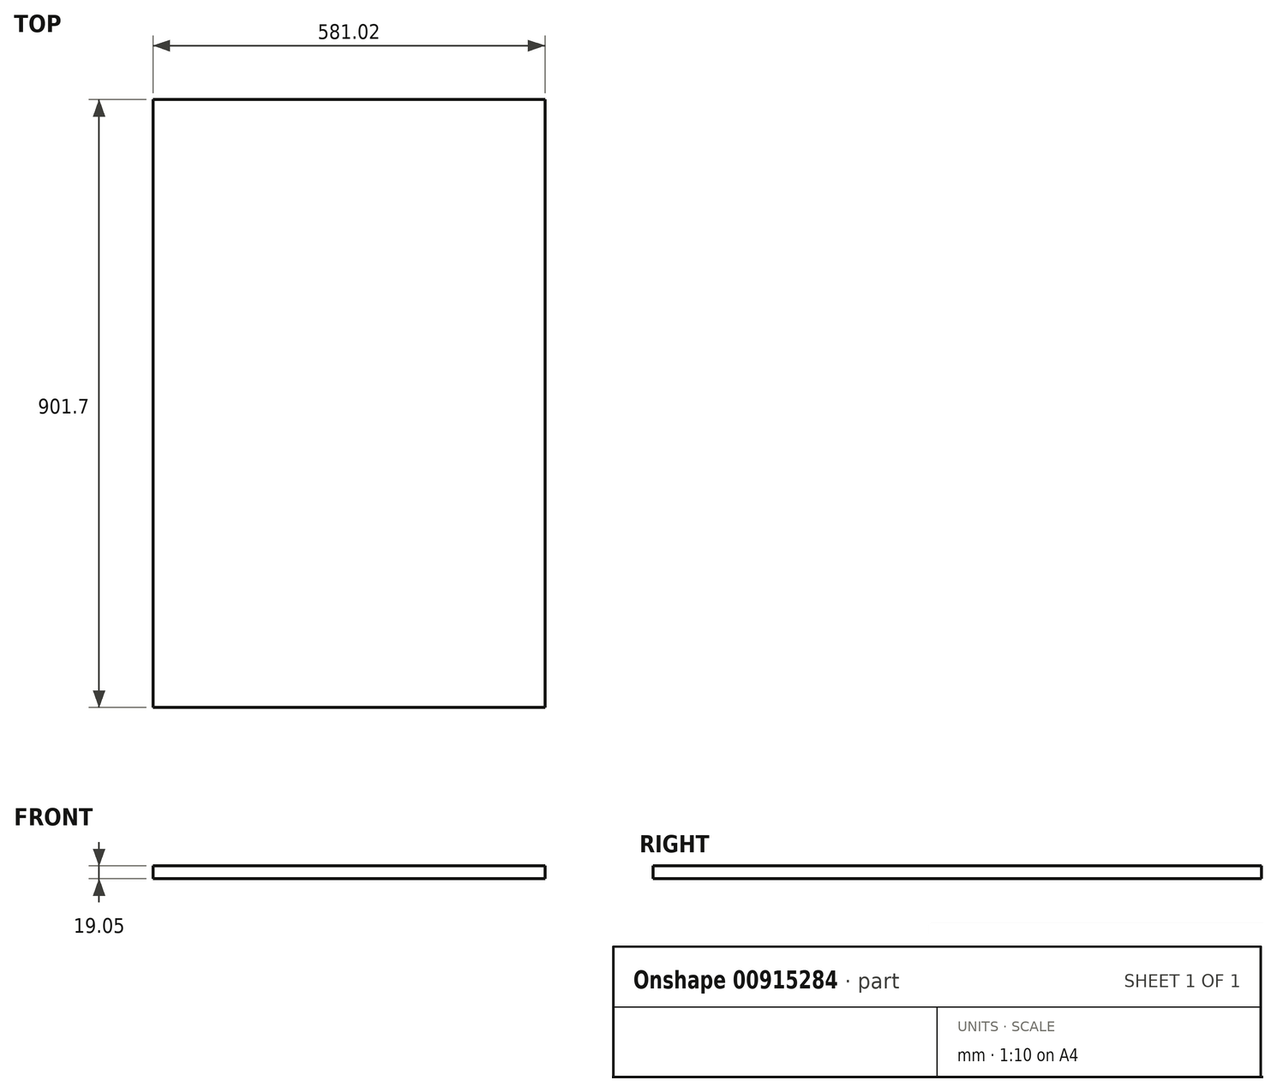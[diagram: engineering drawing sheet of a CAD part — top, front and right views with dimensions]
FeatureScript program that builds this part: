
annotation { "Feature Type Name" : "Feature", "Feature Type Description" : "" }
export const myFeature = defineFeature(function(context is Context, id is Id, definition is map)
    precondition{}
    {
        {
            var Q0;
            Q0=qCreatedBy(makeId("Top.planeOp"),FACE);
            var sketch = newSketch(context, id + "F0", { "sketchPlane" : qUnion([Q0])});
            skLineSegment(sketch, "E0.bottom", {"start": v(290.51, 450.85) * mm, "end": v(-290.51, 450.85) * mm});
            skLineSegment(sketch, "E0.top", {"start": v(290.51, -450.85) * mm, "end": v(-290.51, -450.85) * mm});
            skLineSegment(sketch, "E0.left", {"start": v(290.51, 450.85) * mm, "end": v(290.51, -450.85) * mm});
            skLineSegment(sketch, "E0.right", {"start": v(-290.51, 450.85) * mm, "end": v(-290.51, -450.85) * mm});
            skPoint(sketch, "E0.middle", {"position": v(0, 0) * mm});
            skSolve(sketch);
        }
        {
            var Q0;
            Q0=makeQuery(id+"F0.imprint","IMPRINT",FACE,{"disambiguationData":[TD([[makeQuery(id+"F0.imprint","IMPRINT",EDGE,{"derivedFrom":sQuery(id+"F0.wireOp",EDGE,"E0.bottom")}),1.0]])]});
            extrude(context, id + "F1", {"entities" : qUnion([Q0]), "depth" : 19.05 * mm, "offsetDistance" : 25.4 * mm});
        }
    });
